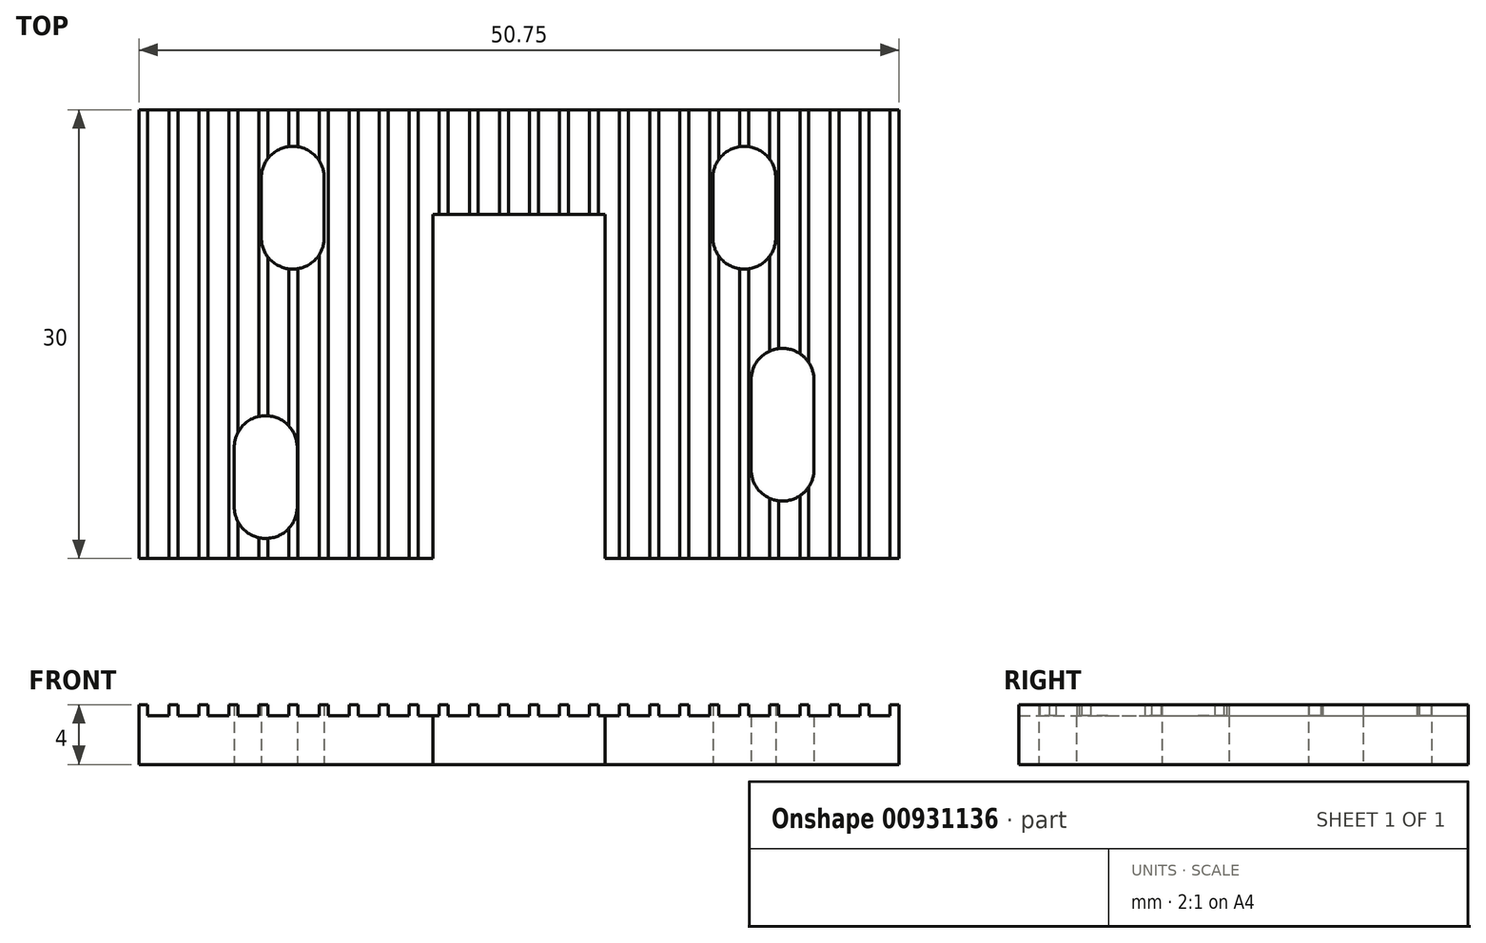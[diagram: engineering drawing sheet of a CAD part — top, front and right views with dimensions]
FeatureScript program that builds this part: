
annotation { "Feature Type Name" : "Feature", "Feature Type Description" : "" }
export const myFeature = defineFeature(function(context is Context, id is Id, definition is map)
    precondition{}
    {
        {
            var Q0;
            Q0=qCreatedBy(makeId("Front.planeOp"),FACE);
            var sketch = newSketch(context, id + "F0", { "sketchPlane" : qUnion([Q0])});
            skLineSegment(sketch, "E0", {"start": v(0, 0) * mm, "end": v(0, 4) * mm});
            skLineSegment(sketch, "E1", {"start": v(0, 4) * mm, "end": v(0.6, 4) * mm});
            skLineSegment(sketch, "E2", {"start": v(0.6, 4) * mm, "end": v(0.6, 3.25) * mm});
            skLineSegment(sketch, "E3", {"start": v(0.6, 3.25) * mm, "end": v(2, 3.25) * mm});
            skLineSegment(sketch, "E4", {"start": v(2, 3.25) * mm, "end": v(2, 4) * mm});
            skLineSegment(sketch, "E5", {"start": v(2, 4) * mm, "end": v(2.6, 4) * mm});
            skLineSegment(sketch, "E6", {"start": v(2.6, 4) * mm, "end": v(2.6, 3.25) * mm});
            skLineSegment(sketch, "E7", {"start": v(2.6, 3.25) * mm, "end": v(4.01, 3.25) * mm});
            skLineSegment(sketch, "E8", {"start": v(4.01, 3.25) * mm, "end": v(4.01, 4) * mm});
            skLineSegment(sketch, "E9", {"start": v(4.01, 4) * mm, "end": v(4.61, 4) * mm});
            skLineSegment(sketch, "E10", {"start": v(4.61, 4) * mm, "end": v(4.61, 3.25) * mm});
            skLineSegment(sketch, "E11.1.0.0", {"start": v(6.02, 4) * mm, "end": v(6.62, 4) * mm});
            skLineSegment(sketch, "E11.1.0.1", {"start": v(6.02, 3.25) * mm, "end": v(6.02, 4) * mm});
            skLineSegment(sketch, "E11.1.0.2", {"start": v(6.62, 4) * mm, "end": v(6.62, 3.25) * mm});
            skLineSegment(sketch, "E11.2.0.0", {"start": v(8.02, 4) * mm, "end": v(8.62, 4) * mm});
            skLineSegment(sketch, "E11.2.0.1", {"start": v(8.02, 3.25) * mm, "end": v(8.02, 4) * mm});
            skLineSegment(sketch, "E11.2.0.2", {"start": v(8.62, 4) * mm, "end": v(8.62, 3.25) * mm});
            skLineSegment(sketch, "E11.3.0.0", {"start": v(10.03, 4) * mm, "end": v(10.63, 4) * mm});
            skLineSegment(sketch, "E11.3.0.1", {"start": v(10.03, 3.25) * mm, "end": v(10.03, 4) * mm});
            skLineSegment(sketch, "E11.3.0.2", {"start": v(10.63, 4) * mm, "end": v(10.63, 3.25) * mm});
            skLineSegment(sketch, "E11.4.0.0", {"start": v(12.04, 4) * mm, "end": v(12.64, 4) * mm});
            skLineSegment(sketch, "E11.4.0.1", {"start": v(12.04, 3.25) * mm, "end": v(12.04, 4) * mm});
            skLineSegment(sketch, "E11.4.0.2", {"start": v(12.64, 4) * mm, "end": v(12.64, 3.25) * mm});
            skLineSegment(sketch, "E11.5.0.0", {"start": v(14.04, 4) * mm, "end": v(14.64, 4) * mm});
            skLineSegment(sketch, "E11.5.0.1", {"start": v(14.04, 3.25) * mm, "end": v(14.04, 4) * mm});
            skLineSegment(sketch, "E11.5.0.2", {"start": v(14.64, 4) * mm, "end": v(14.64, 3.25) * mm});
            skLineSegment(sketch, "E11.6.0.0", {"start": v(16.05, 4) * mm, "end": v(16.65, 4) * mm});
            skLineSegment(sketch, "E11.6.0.1", {"start": v(16.05, 3.25) * mm, "end": v(16.05, 4) * mm});
            skLineSegment(sketch, "E11.6.0.2", {"start": v(16.65, 4) * mm, "end": v(16.65, 3.25) * mm});
            skLineSegment(sketch, "E11.7.0.0", {"start": v(18.05, 4) * mm, "end": v(18.65, 4) * mm});
            skLineSegment(sketch, "E11.7.0.1", {"start": v(18.05, 3.25) * mm, "end": v(18.05, 4) * mm});
            skLineSegment(sketch, "E11.7.0.2", {"start": v(18.65, 4) * mm, "end": v(18.65, 3.25) * mm});
            skLineSegment(sketch, "E11.8.0.0", {"start": v(20.06, 4) * mm, "end": v(20.66, 4) * mm});
            skLineSegment(sketch, "E11.8.0.1", {"start": v(20.06, 3.25) * mm, "end": v(20.06, 4) * mm});
            skLineSegment(sketch, "E11.8.0.2", {"start": v(20.66, 4) * mm, "end": v(20.66, 3.25) * mm});
            skLineSegment(sketch, "E11.9.0.0", {"start": v(22.07, 4) * mm, "end": v(22.67, 4) * mm});
            skLineSegment(sketch, "E11.9.0.1", {"start": v(22.07, 3.25) * mm, "end": v(22.07, 4) * mm});
            skLineSegment(sketch, "E11.9.0.2", {"start": v(22.67, 4) * mm, "end": v(22.67, 3.25) * mm});
            skLineSegment(sketch, "E11.10.0.0", {"start": v(24.07, 4) * mm, "end": v(24.67, 4) * mm});
            skLineSegment(sketch, "E11.10.0.1", {"start": v(24.07, 3.25) * mm, "end": v(24.07, 4) * mm});
            skLineSegment(sketch, "E11.10.0.2", {"start": v(24.67, 4) * mm, "end": v(24.67, 3.25) * mm});
            skLineSegment(sketch, "E11.11.0.0", {"start": v(26.08, 4) * mm, "end": v(26.68, 4) * mm});
            skLineSegment(sketch, "E11.11.0.1", {"start": v(26.08, 3.25) * mm, "end": v(26.08, 4) * mm});
            skLineSegment(sketch, "E11.11.0.2", {"start": v(26.68, 4) * mm, "end": v(26.68, 3.25) * mm});
            skLineSegment(sketch, "E11.12.0.0", {"start": v(28.08, 4) * mm, "end": v(28.68, 4) * mm});
            skLineSegment(sketch, "E11.12.0.1", {"start": v(28.08, 3.25) * mm, "end": v(28.08, 4) * mm});
            skLineSegment(sketch, "E11.12.0.2", {"start": v(28.68, 4) * mm, "end": v(28.68, 3.25) * mm});
            skLineSegment(sketch, "E11.13.0.0", {"start": v(30.1, 4) * mm, "end": v(30.7, 4) * mm});
            skLineSegment(sketch, "E11.13.0.1", {"start": v(30.1, 3.25) * mm, "end": v(30.1, 4) * mm});
            skLineSegment(sketch, "E11.13.0.2", {"start": v(30.7, 4) * mm, "end": v(30.7, 3.25) * mm});
            skLineSegment(sketch, "E11.14.0.0", {"start": v(32.1, 4) * mm, "end": v(32.7, 4) * mm});
            skLineSegment(sketch, "E11.14.0.1", {"start": v(32.1, 3.25) * mm, "end": v(32.1, 4) * mm});
            skLineSegment(sketch, "E11.14.0.2", {"start": v(32.7, 4) * mm, "end": v(32.7, 3.25) * mm});
            skLineSegment(sketch, "E11.15.0.0", {"start": v(34.1, 4) * mm, "end": v(34.7, 4) * mm});
            skLineSegment(sketch, "E11.15.0.1", {"start": v(34.1, 3.25) * mm, "end": v(34.1, 4) * mm});
            skLineSegment(sketch, "E11.15.0.2", {"start": v(34.7, 4) * mm, "end": v(34.7, 3.25) * mm});
            skLineSegment(sketch, "E11.16.0.0", {"start": v(36.1, 4) * mm, "end": v(36.7, 4) * mm});
            skLineSegment(sketch, "E11.16.0.1", {"start": v(36.1, 3.25) * mm, "end": v(36.1, 4) * mm});
            skLineSegment(sketch, "E11.16.0.2", {"start": v(36.7, 4) * mm, "end": v(36.7, 3.25) * mm});
            skLineSegment(sketch, "E11.17.0.0", {"start": v(38.11, 4) * mm, "end": v(38.71, 4) * mm});
            skLineSegment(sketch, "E11.17.0.1", {"start": v(38.11, 3.25) * mm, "end": v(38.11, 4) * mm});
            skLineSegment(sketch, "E11.17.0.2", {"start": v(38.71, 4) * mm, "end": v(38.71, 3.25) * mm});
            skLineSegment(sketch, "E11.18.0.0", {"start": v(40.12, 4) * mm, "end": v(40.72, 4) * mm});
            skLineSegment(sketch, "E11.18.0.1", {"start": v(40.12, 3.25) * mm, "end": v(40.12, 4) * mm});
            skLineSegment(sketch, "E11.18.0.2", {"start": v(40.72, 4) * mm, "end": v(40.72, 3.25) * mm});
            skLineSegment(sketch, "E11.19.0.0", {"start": v(42.13, 4) * mm, "end": v(42.73, 4) * mm});
            skLineSegment(sketch, "E11.19.0.1", {"start": v(42.13, 3.25) * mm, "end": v(42.13, 4) * mm});
            skLineSegment(sketch, "E11.19.0.2", {"start": v(42.73, 4) * mm, "end": v(42.73, 3.25) * mm});
            skLineSegment(sketch, "E11.20.0.0", {"start": v(44.13, 4) * mm, "end": v(44.73, 4) * mm});
            skLineSegment(sketch, "E11.20.0.1", {"start": v(44.13, 3.25) * mm, "end": v(44.13, 4) * mm});
            skLineSegment(sketch, "E11.20.0.2", {"start": v(44.73, 4) * mm, "end": v(44.73, 3.25) * mm});
            skLineSegment(sketch, "E11.21.0.0", {"start": v(46.14, 4) * mm, "end": v(46.74, 4) * mm});
            skLineSegment(sketch, "E11.21.0.1", {"start": v(46.14, 3.25) * mm, "end": v(46.14, 4) * mm});
            skLineSegment(sketch, "E11.21.0.2", {"start": v(46.74, 4) * mm, "end": v(46.74, 3.25) * mm});
            skLineSegment(sketch, "E12", {"start": v(6.62, 3.25) * mm, "end": v(8.02, 3.25) * mm});
            skLineSegment(sketch, "E13", {"start": v(8.62, 3.25) * mm, "end": v(10.03, 3.25) * mm});
            skLineSegment(sketch, "E14", {"start": v(10.63, 3.25) * mm, "end": v(12.04, 3.25) * mm});
            skLineSegment(sketch, "E15", {"start": v(12.64, 3.25) * mm, "end": v(14.04, 3.25) * mm});
            skLineSegment(sketch, "E16", {"start": v(14.64, 3.25) * mm, "end": v(16.05, 3.25) * mm});
            skLineSegment(sketch, "E17", {"start": v(16.65, 3.25) * mm, "end": v(18.05, 3.25) * mm});
            skLineSegment(sketch, "E18", {"start": v(18.65, 3.25) * mm, "end": v(20.06, 3.25) * mm});
            skLineSegment(sketch, "E19", {"start": v(20.66, 3.25) * mm, "end": v(22.07, 3.25) * mm});
            skLineSegment(sketch, "E20", {"start": v(22.67, 3.25) * mm, "end": v(24.07, 3.25) * mm});
            skLineSegment(sketch, "E21", {"start": v(24.67, 3.25) * mm, "end": v(26.08, 3.25) * mm});
            skLineSegment(sketch, "E22", {"start": v(26.68, 3.25) * mm, "end": v(28.08, 3.25) * mm});
            skLineSegment(sketch, "E23", {"start": v(28.68, 3.25) * mm, "end": v(30.1, 3.25) * mm});
            skLineSegment(sketch, "E24", {"start": v(30.7, 3.25) * mm, "end": v(32.1, 3.25) * mm});
            skLineSegment(sketch, "E25", {"start": v(32.7, 3.25) * mm, "end": v(34.1, 3.25) * mm});
            skLineSegment(sketch, "E26", {"start": v(34.7, 3.25) * mm, "end": v(36.1, 3.25) * mm});
            skLineSegment(sketch, "E27", {"start": v(36.7, 3.25) * mm, "end": v(38.11, 3.25) * mm});
            skLineSegment(sketch, "E28", {"start": v(38.71, 3.25) * mm, "end": v(40.12, 3.25) * mm});
            skLineSegment(sketch, "E29", {"start": v(40.72, 3.25) * mm, "end": v(42.13, 3.25) * mm});
            skLineSegment(sketch, "E30", {"start": v(42.73, 3.25) * mm, "end": v(44.13, 3.25) * mm});
            skLineSegment(sketch, "E31", {"start": v(44.73, 3.25) * mm, "end": v(46.14, 3.25) * mm});
            skLineSegment(sketch, "E32", {"start": v(50.75, 0) * mm, "end": v(0, 0) * mm});
            skLineSegment(sketch, "E33.0.22.0", {"start": v(48.14, 4) * mm, "end": v(48.74, 4) * mm});
            skLineSegment(sketch, "E33.3.22.0", {"start": v(48.14, 3.25) * mm, "end": v(48.14, 4) * mm});
            skLineSegment(sketch, "E33.6.22.0", {"start": v(48.74, 4) * mm, "end": v(48.74, 3.25) * mm});
            skLineSegment(sketch, "E33.0.23.0", {"start": v(50.15, 4) * mm, "end": v(50.75, 4) * mm});
            skLineSegment(sketch, "E33.3.23.0", {"start": v(50.15, 3.25) * mm, "end": v(50.15, 4) * mm});
            skLineSegment(sketch, "E33.6.23.0", {"start": v(50.75, 4) * mm, "end": v(50.75, 3.25) * mm});
            skLineSegment(sketch, "E34", {"start": v(46.74, 3.25) * mm, "end": v(48.14, 3.25) * mm});
            skLineSegment(sketch, "E35", {"start": v(48.74, 3.25) * mm, "end": v(50.15, 3.25) * mm});
            skLineSegment(sketch, "E36", {"start": v(4.61, 3.25) * mm, "end": v(6.02, 3.25) * mm});
            skLineSegment(sketch, "E37", {"start": v(8.97, 13.53) * mm, "end": v(13.97, 13.53) * mm});
            skLineSegment(sketch, "E38", {"start": v(13.97, 13.53) * mm, "end": v(13.97, 13.47) * mm});
            skLineSegment(sketch, "E39", {"start": v(13.97, 13.47) * mm, "end": v(13.97, 8.47) * mm});
            skLineSegment(sketch, "E40", {"start": v(13.97, 8.47) * mm, "end": v(18.97, 8.47) * mm});
            skLineSegment(sketch, "E41", {"start": v(18.97, 8.47) * mm, "end": v(18.97, 13.47) * mm});
            skLineSegment(sketch, "E42", {"start": v(18.97, 13.47) * mm, "end": v(23.97, 13.47) * mm});
            skLineSegment(sketch, "E43", {"start": v(6.32, 4) * mm, "end": v(6.32, 5.33) * mm});
            skLineSegment(sketch, "E44", {"start": v(8.32, 4) * mm, "end": v(8.32, 5.33) * mm});
            skLineSegment(sketch, "E45", {"start": v(8.32, 5.33) * mm, "end": v(6.32, 5.33) * mm});
            skLineSegment(sketch, "E46", {"start": v(50.75, 3.25) * mm, "end": v(50.75, 0) * mm});
            skSolve(sketch);
        }
        {
            var Q0;
            Q0=makeQuery(id+"F0.imprint","IMPRINT",FACE,{"disambiguationData":[TD([[makeQuery(id+"F0.imprint","IMPRINT",EDGE,{"derivedFrom":sQuery(id+"F0.wireOp",EDGE,"E0")}),-1.0]])]});
            extrude(context, id + "F1", {"entities" : qUnion([Q0]), "depth" : 30 * mm, "offsetDistance" : 25 * mm});
        }
        {
            var Q0;
            Q0=makeQuery(id+"F1.opExtrude","SWEPT_FACE",FACE,{"disambiguationData":[OSD([sQuery(id+"F0.wireOp",EDGE,"E32")])]});
            var sketch = newSketch(context, id + "F2", { "sketchPlane" : qUnion([Q0])});
            skLineSegment(sketch, "E47", {"start": v(25.37, 30) * mm, "end": v(25.37, 7) * mm});
            skLineSegment(sketch, "E48", {"start": v(19.62, 30) * mm, "end": v(19.62, 7) * mm});
            skLineSegment(sketch, "E49", {"start": v(19.62, 7) * mm, "end": v(25.37, 7) * mm});
            skLineSegment(sketch, "E50", {"start": v(25.37, 7) * mm, "end": v(31.12, 7) * mm});
            skLineSegment(sketch, "E51", {"start": v(31.12, 7) * mm, "end": v(31.12, 30) * mm});
            skPoint(sketch, "E52.orphan", {"position": v(25.37, 0) * mm});
            skLineSegment(sketch, "E53.bottom", {"start": v(8.17, 8.55) * mm, "end": v(12.37, 8.55) * mm});
            skLineSegment(sketch, "E53.top", {"start": v(8.17, 4.55) * mm, "end": v(12.37, 4.55) * mm});
            skLineSegment(sketch, "E53.left", {"start": v(12.37, 8.55) * mm, "end": v(12.37, 4.55) * mm});
            skLineSegment(sketch, "E53.right", {"start": v(8.17, 8.55) * mm, "end": v(8.17, 4.55) * mm});
            skLineSegment(sketch, "E54.bottom", {"start": v(38.32, 8.55) * mm, "end": v(42.52, 8.55) * mm});
            skLineSegment(sketch, "E54.top", {"start": v(38.32, 4.55) * mm, "end": v(42.52, 4.55) * mm});
            skLineSegment(sketch, "E54.left", {"start": v(38.32, 8.55) * mm, "end": v(38.32, 4.55) * mm});
            skLineSegment(sketch, "E54.right", {"start": v(42.52, 8.55) * mm, "end": v(42.52, 4.55) * mm});
            skArc(sketch, "E55", {"start": v(8.17, 8.55) * mm, "mid": v(10.27, 10.65) * mm, "end": v(12.37, 8.55) * mm});
            skArc(sketch, "E56", {"start": v(8.17, 4.55) * mm, "mid": v(10.27, 2.45) * mm, "end": v(12.37, 4.55) * mm});
            skArc(sketch, "E57", {"start": v(38.32, 8.55) * mm, "mid": v(40.42, 10.65) * mm, "end": v(42.52, 8.55) * mm});
            skArc(sketch, "E58", {"start": v(42.52, 4.55) * mm, "mid": v(40.42, 2.45) * mm, "end": v(38.32, 4.55) * mm});
            skLineSegment(sketch, "E59.bottom", {"start": v(6.37, 26.55) * mm, "end": v(10.57, 26.55) * mm});
            skLineSegment(sketch, "E59.top", {"start": v(6.37, 22.55) * mm, "end": v(10.57, 22.55) * mm});
            skLineSegment(sketch, "E59.left", {"start": v(10.57, 26.55) * mm, "end": v(10.57, 22.55) * mm});
            skLineSegment(sketch, "E59.right", {"start": v(6.37, 26.55) * mm, "end": v(6.37, 22.55) * mm});
            skArc(sketch, "E60", {"start": v(6.37, 26.55) * mm, "mid": v(8.47, 28.65) * mm, "end": v(10.57, 26.55) * mm});
            skArc(sketch, "E61", {"start": v(6.37, 22.55) * mm, "mid": v(8.47, 20.45) * mm, "end": v(10.57, 22.55) * mm});
            skLineSegment(sketch, "E62.bottom", {"start": v(40.87, 24.05) * mm, "end": v(45.07, 24.05) * mm});
            skLineSegment(sketch, "E62.top", {"start": v(40.87, 18.05) * mm, "end": v(45.07, 18.05) * mm});
            skLineSegment(sketch, "E62.left", {"start": v(45.07, 24.05) * mm, "end": v(45.07, 18.05) * mm});
            skLineSegment(sketch, "E62.right", {"start": v(40.87, 24.05) * mm, "end": v(40.87, 18.05) * mm});
            skArc(sketch, "E63", {"start": v(40.87, 24.05) * mm, "mid": v(42.97, 26.15) * mm, "end": v(45.07, 24.05) * mm});
            skArc(sketch, "E64", {"start": v(40.87, 18.05) * mm, "mid": v(42.97, 15.95) * mm, "end": v(45.07, 18.05) * mm});
            skSolve(sketch);
        }
        {
            var Q0;
            {var subQ0=sQuery(id+"F2.wireOp",EDGE,"E47");Q0=makeQuery(id+"F2.imprint","IMPRINT",FACE,{"disambiguationData":[TD([[makeQuery(id+"F2.imprint","IMPRINT",EDGE,{"derivedFrom":subQ0}),-1.0]])]});}
            var Q1;
            {var subQ0=sQuery(id+"F2.wireOp",EDGE,"E47");Q1=makeQuery(id+"F2.imprint","IMPRINT",FACE,{"disambiguationData":[TD([[makeQuery(id+"F2.imprint","IMPRINT",EDGE,{"derivedFrom":subQ0}),1.0]])]});}
            extrude(context, id + "F3", {"entities" : qUnion([Q0, Q1]), "operationType" : NewBodyOperationType.REMOVE, "endBound" : BoundingType.UP_TO_NEXT, "oppositeDirection" : true, "depth" : 25 * mm, "offsetDistance" : 25 * mm});
        }
        {
            var Q0;
            Q0=qSketchRegion(id+"F2",true);
            extrude(context, id + "F4", {"entities" : qUnion([Q0]), "operationType" : NewBodyOperationType.REMOVE, "endBound" : BoundingType.UP_TO_NEXT, "oppositeDirection" : true, "depth" : 25 * mm, "offsetDistance" : 25 * mm});
        }
    });
